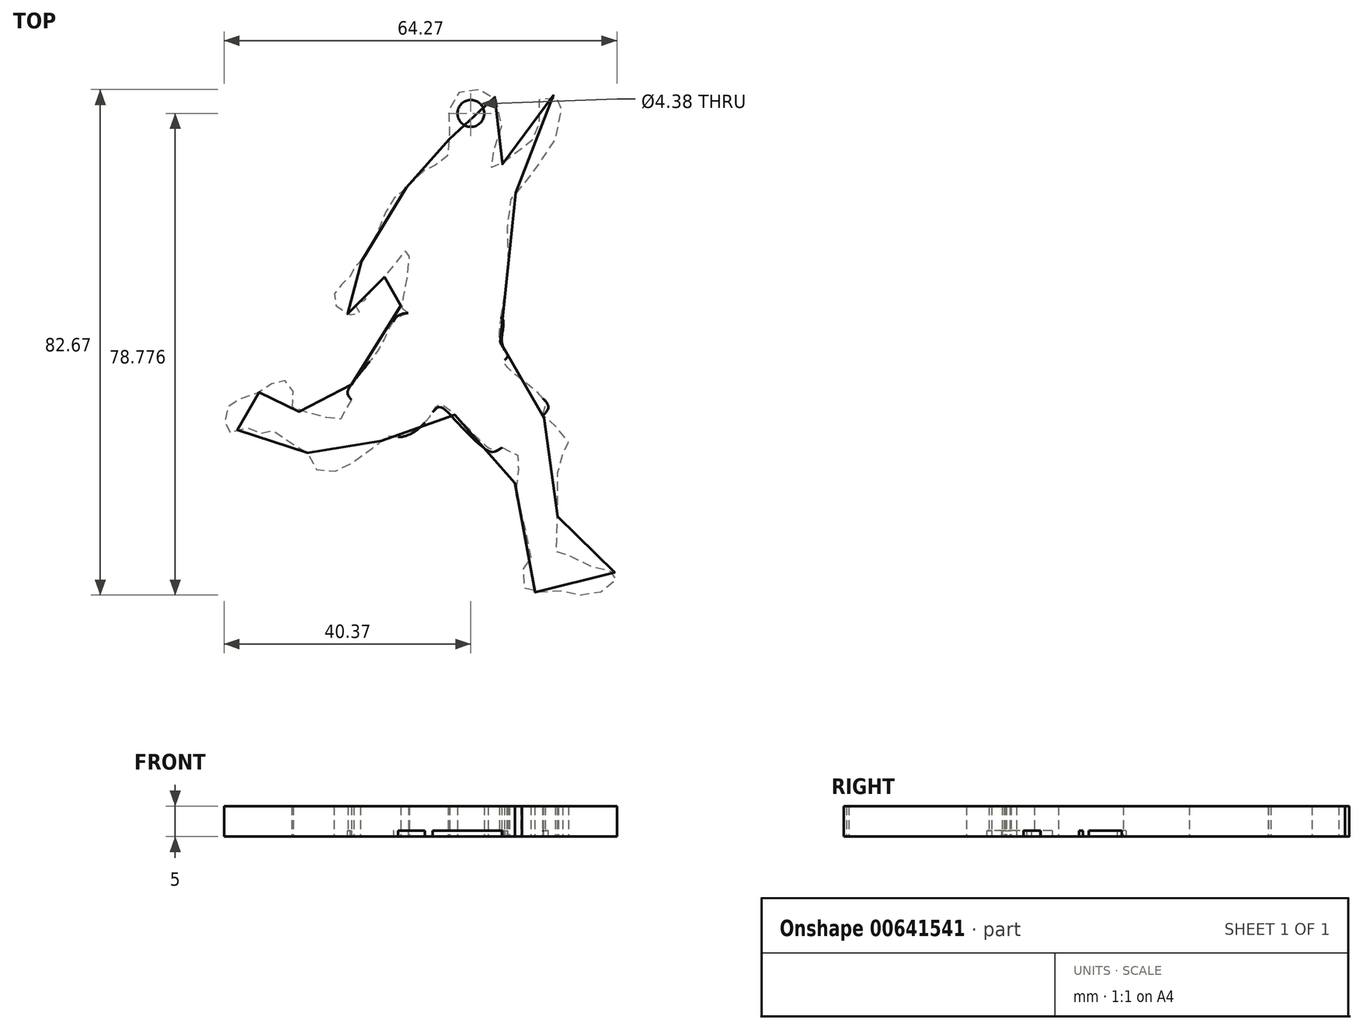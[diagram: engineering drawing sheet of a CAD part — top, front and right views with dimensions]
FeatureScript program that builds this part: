
annotation { "Feature Type Name" : "Feature", "Feature Type Description" : "" }
export const myFeature = defineFeature(function(context is Context, id is Id, definition is map)
    precondition{}
    {
        {
            var Q0;
            Q0=qCreatedBy(makeId("Top.planeOp"),FACE);
            var sketch = newSketch(context, id + "F0", { "sketchPlane" : qUnion([Q0])});
            skFitSpline(sketch, "E0", {"points": [v(-10.56, 44.59) * mm, v(-13, 42.34) * mm, v(-14.49, 39.16) * mm, v(-15.8, 36.36) * mm, v(-17.67, 32.8) * mm, v(-19.54, 30.94) * mm, v(-20.1, 29.44) * mm, v(-21.97, 28.13) * mm, v(-22.34, 26.45) * mm, v(-21.22, 24.4) * mm, v(-18.04, 23.83) * mm, v(-19.16, 25.33) * mm, v(-17.67, 25.9) * mm, v(-17.1, 26.64) * mm, v(-15.05, 29.26) * mm, v(-13.55, 30.56) * mm, v(-10.38, 34.5) * mm, v(-10.19, 32.25) * mm, v(-11.12, 26.64) * mm, v(-11.3, 24.96) * mm, v(-10.19, 24.2) * mm, v(-12.06, 23.27) * mm, v(-15.05, 18.23) * mm, v(-20.1, 11.12) * mm, v(-19.54, 9.81) * mm, v(-22.15, 6.26) * mm, v(-24.2, 7.38) * mm, v(-27.95, 7.94) * mm, v(-29.26, 8.88) * mm, v(-29.07, 11.5) * mm, v(-30.2, 13) * mm, v(-32.06, 12.8) * mm, v(-33.37, 11.87) * mm, v(-36.55, 10.38) * mm, v(-38.42, 9.81) * mm, v(-40.29, 7.76) * mm, v(-40.1, 5.7) * mm, v(-39.54, 4.58) * mm, v(-36.55, 5.33) * mm, v(-34.5, 4.4) * mm, v(-33, 5.14) * mm, v(-30.94, 3.65) * mm, v(-27.01, 1.59) * mm, v(-25.33, -1.4) * mm, v(-22.15, -1.78) * mm, v(-18.79, 0) * mm, v(-14.49, 3.27) * mm, v(-13, 4.2) * mm, v(-11.87, 3.83) * mm, v(-6.82, 7.01) * mm, v(-4.77, 9.07) * mm, v(3.46, 1.78) * mm, v(5.33, 2.15) * mm, v(8.13, 0) * mm, v(7.2, -3.46) * mm, v(9.81, -15.8) * mm, v(8.7, -17.48) * mm, v(9.07, -21.22) * mm, v(13.93, -21.22) * mm, v(17.3, -21.97) * mm, v(22.53, -20.84) * mm, v(23.83, -18.6) * mm, v(21.03, -17.85) * mm, v(15.6, -15.42) * mm, v(13.93, -14.86) * mm, v(14.11, -12.24) * mm, v(14.49, 0) * mm, v(15.6, 1.78) * mm, v(15.6, 4.02) * mm, v(11.87, 7.2) * mm, v(12.06, 9.63) * mm, v(5.51, 15.98) * mm, v(6.08, 17.3) * mm, v(4.95, 18.79) * mm, v(6.26, 32.25) * mm, v(6.08, 41.4) * mm, v(10, 46.83) * mm, v(15.05, 56.36) * mm, v(14.3, 58.6) * mm, v(14.3, 58.98) * mm, v(12.24, 59.91) * mm, v(10.56, 55.99) * mm, v(11.68, 54.12) * mm, v(5.7, 49.07) * mm, v(4.58, 47.95) * mm, v(2.9, 48.14) * mm, v(4.2, 51.5) * mm, v(4.95, 56.18) * mm, v(3.08, 60.29) * mm, v(0, 60.47) * mm, v(-2.34, 59.91) * mm, v(-3.65, 56.74) * mm, v(-3.46, 51.5) * mm, v(-3.83, 49.82) * mm, v(-5.14, 49.26) * mm, v(-6.45, 47.39) * mm, v(-7.57, 47.39) * mm, v(-10.56, 44.59) * mm]});
            skCircle(sketch, "E1", {"center": v(0, 56.74) * mm, "radius": 2.2 * mm});
            skSolve(sketch);
        }
        {
            var Q0;
            Q0=makeQuery(id+"F0.imprint","IMPRINT",FACE,{"disambiguationData":[TD([[makeQuery(id+"F0.imprint","IMPRINT",EDGE,{"derivedFrom":sQuery(id+"F0.wireOp",EDGE,"E0")}),1.0]])]});
            extrude(context, id + "F1", {"entities" : qUnion([Q0]), "depth" : 5 * mm, "offsetDistance" : 25.4 * mm});
        }
        {
            var Q0;
            Q0=qCreatedBy(makeId("Top.planeOp"),FACE);
            var sketch = newSketch(context, id + "F2", { "sketchPlane" : qUnion([Q0])});
            skFitSpline(sketch, "E2", {"points": [v(-10.22, 24.1) * mm, v(-12.36, 23.2) * mm, v(-15.02, 18.05) * mm, v(-20, 11.65) * mm, v(-19.65, 10.05) * mm, v(-12.53, 4.18) * mm, v(-11.47, 3.82) * mm, v(-8.45, 5.25) * mm, v(-5.42, 8.62) * mm, v(-3.47, 7.56) * mm, v(2.93, 1.51) * mm, v(5.25, 2.22) * mm, v(11.82, 7.38) * mm, v(12.36, 9.51) * mm, v(5.07, 15.56) * mm, v(5.78, 16.62) * mm, v(5.96, 17.16) * mm, v(5.07, 19.3) * mm, v(5.25, 23.03) * mm, v(1.69, 23.74) * mm, v(-10.22, 24.1) * mm]});
            skSolve(sketch);
        }
        {
            var Q0;
            Q0 = qSketchRegion(id + "F2", true);
            extrude(context, id + "F3", {"entities" : qUnion([Q0]), "operationType" : NewBodyOperationType.ADD, "depth" : 1 * mm, "offsetDistance" : 25.4 * mm});
        }
    });
